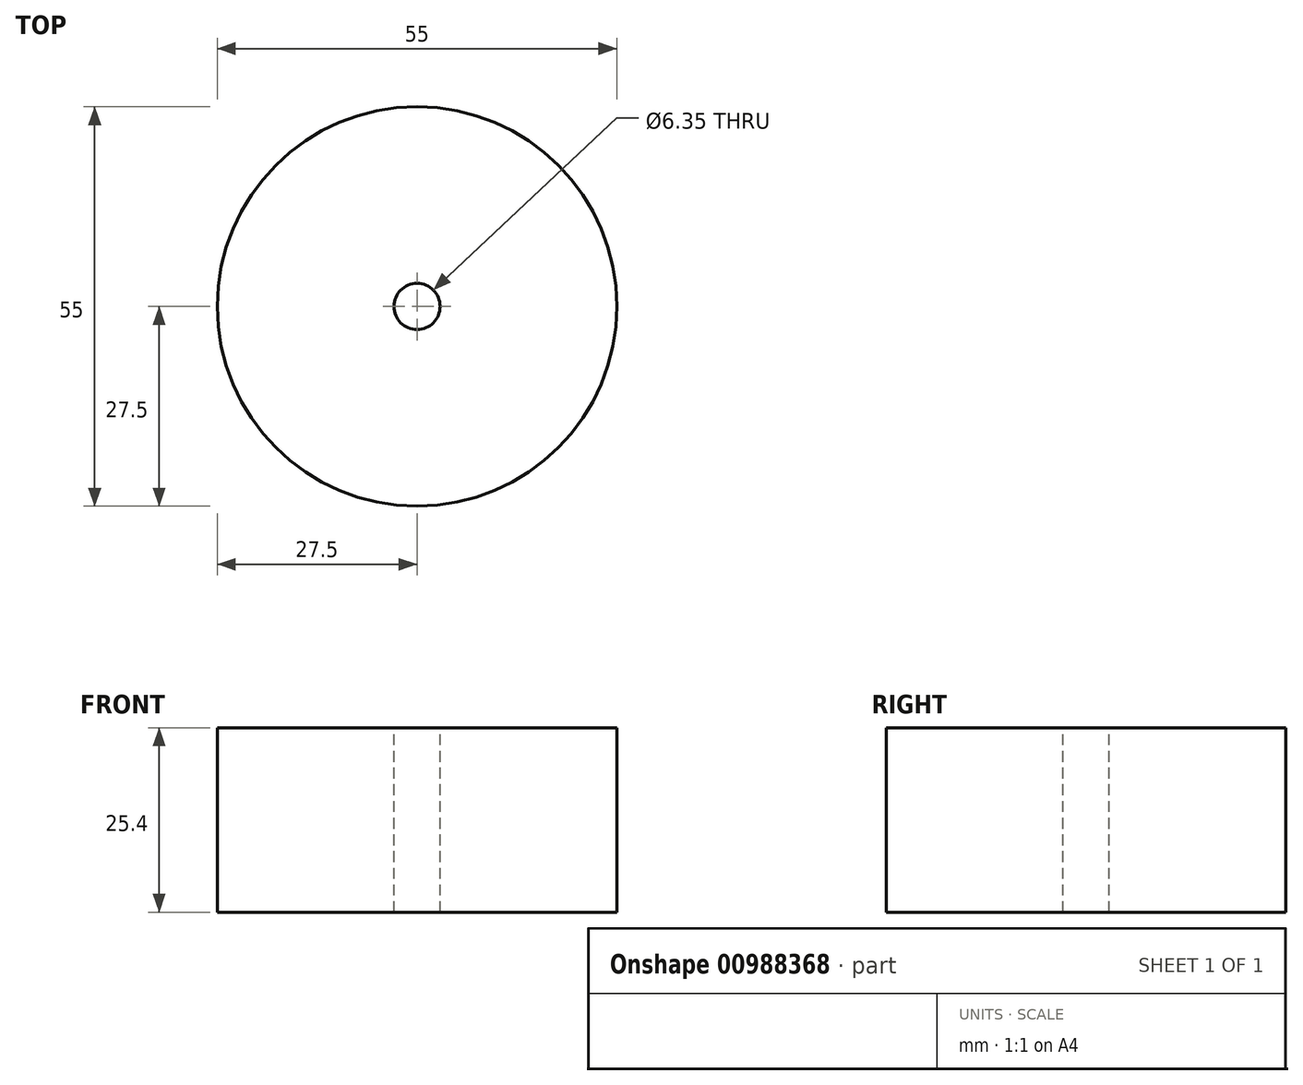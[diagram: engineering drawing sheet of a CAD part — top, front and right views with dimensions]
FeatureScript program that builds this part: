
annotation { "Feature Type Name" : "Feature", "Feature Type Description" : "" }
export const myFeature = defineFeature(function(context is Context, id is Id, definition is map)
    precondition{}
    {
        {
            var Q0;
            Q0=qCreatedBy(makeId("Top.planeOp"),FACE);
            var sketch = newSketch(context, id + "F0", { "sketchPlane" : qUnion([Q0])});
            skCircle(sketch, "E0", {"center": v(0, 0) * mm, "radius": 27.5 * mm});
            skSolve(sketch);
        }
        {
            var Q0;
            Q0=makeQuery(id+"F0.imprint","IMPRINT",FACE,{"disambiguationData":[TD([[makeQuery(id+"F0.imprint","IMPRINT",EDGE,{"derivedFrom":sQuery(id+"F0.wireOp",EDGE,"E0")}),1.0]])]});
            extrude(context, id + "F1", {"entities" : qUnion([Q0]), "depth" : 25.4 * mm, "offsetDistance" : 25.4 * mm});
        }
        {
            var Q0;
            Q0=makeQuery(id+"F1.opExtrude","CAP_FACE",FACE,{"disambiguationData":[OSD([sQuery(id+"F0.wireOp",EDGE,"E0")])],"isStart":false});
            var sketch = newSketch(context, id + "F2", { "sketchPlane" : qUnion([Q0])});
            skLineSegment(sketch, "E1", {"start": v(-27.43, 2.02) * mm, "end": v(10.06, -25.6) * mm, "construction": true});
            skLineSegment(sketch, "E2", {"start": v(10.06, -25.6) * mm, "end": v(27.43, -2.02) * mm, "construction": true});
            skLineSegment(sketch, "E3", {"start": v(27.43, -2.02) * mm, "end": v(-10.06, 25.6) * mm, "construction": true});
            skLineSegment(sketch, "E4", {"start": v(-10.06, 25.6) * mm, "end": v(-27.43, 2.02) * mm, "construction": true});
            skLineSegment(sketch, "E5", {"start": v(-10.06, 25.6) * mm, "end": v(10.06, -25.6) * mm, "construction": true});
            skLineSegment(sketch, "E6", {"start": v(27.43, -2.02) * mm, "end": v(-27.43, 2.02) * mm, "construction": true});
            skCircle(sketch, "E7", {"center": v(0, 0) * mm, "radius": 10.16 * mm, "construction": true});
            skCircle(sketch, "E8", {"center": v(0, 0) * mm, "radius": 3.18 * mm});
            skSolve(sketch);
        }
        {
            var Q0;
            Q0=makeQuery(id+"F2.imprint","IMPRINT",FACE,{"disambiguationData":[TD([[makeQuery(id+"F2.imprint","IMPRINT",EDGE,{"derivedFrom":sQuery(id+"F2.wireOp",EDGE,"E8")}),1.0]])]});
            extrude(context, id + "F3", {"entities" : qUnion([Q0]), "operationType" : NewBodyOperationType.REMOVE, "oppositeDirection" : true, "depth" : 25.4 * mm, "offsetDistance" : 25.4 * mm});
        }
    });
